# Revit family: IS_TonicII_R4340_BIM_DE
name_source: partatom
category: Plumbing Fixtures
revit_build: Autodesk Revit MEP 2016 (Build: 20161004_0715(x64)
units: mm (PartAtom-declared; Revit-internal decimal feet)

## family parameters
Always vertical = No
Cut with Voids When Loaded = No
OmniClass Number = 23.45.05.14.17.11
OmniClass Title = Shower Compartments
Part Type = Normal
Room Calculation Point = No
Round Connector Dimension = Use Diameter
Shared = No
Work Plane-Based = No

## types (1)
- R4340WG - TONIC II shelf 350x440mm
    Accessories = www.idealstandard.de\ersatzteile
    AreaUnits = millimeters
    AssetType = Fixed
    BIMObjectName = ISI_IdealStandard_Furniture_Tonic Ii_R4340WG
    BIMobject category = Storage
    BOSUseNativeGeometries = 1
    BarCode = 3391500573024
    Brand = Ideal Standard
    Brand url = http://www.idealstandard.co.uk
    Color = Glossy White
    ConnectionType = Mechanical
    CurrencyUnit = €
    Date of publishing = 06/11/2017
    Description = R4340WG TONIC II shelf 350x440mm
    DurationUnit = year
    EAN code = https://3391500573024
    Edition number = 1
    ExpectedLife = 25
    Features = TONIC II shelf 350x440mm
    Finish = Glossy White
    IFC Classification = Sanitary Terminal
    IfcExportAs = Sanitary Terminal Type
    IfcExportType = VanityUnits
    InstallationInstructions = www.idealstandard.de\produkte
    LinearUnits = millimeters
    MainColor = Glossy White
    MaintenanceInformation = www.idealstandard.de\produkte
    Manufacturer name = Ideal Standard
    ManufacturerURL = www.idealstandard.com
    Model = R4340WG
    ModelNumber = R4340WG
    ModelReference = TONIC II shelf 350x440mm
    NBS Reference Code = 35-75-94
    NBS Reference Description = Vanity Units
    Name = Furniture_Tonic Ii_R4340WG_IdealStandard
    NettWeight = 5 kg
    Nominal height = 170
    Nominal width = 350
    NominalDepth = 440 mm  [stored 1.44357 ft]
    NominalHeight = 170 mm
    NominalLength = 440 mm  [stored 1.44357 ft]
    NominalWidth = 347 mm
    Product Guid = 3416c0c4-0ad5-4c75-99fe-f1d4c0795bb9
    Product SKU = R4340
    Product data url = https://bimobject.com
    Product family = TONIC II
    Product group = Furniture
    Product name = TONIC II 350 MM OPEN SHELF GLASS WHITE
    Product url = http://www.idealspec.fr
    ProductInformation = www.idealstandard.de/produkte
    QR code = http://bimobject.com
    Shape = Rectangular
    Size = 170 x 440 x 347mm
    Space = Internal
    SpareParts = www.idealstandard.de/ersatzteile
    Technical description = http://www.idealspec.fr
    URL = www.idealstandard.com
    Uniclass 1.4 Code = L72121
    Uniclass 1.4 Description = Vanity units
    Uniclass 2.0 Code = PR-35-75-94
    Uniclass 2.0 Description = Vanity Units
    Uniclass 2015 Code = Pr_40_20_76_94
    Uniclass 2015 Name = Vanity units
    Uniclass2015Code = Pr_40_20_76_94
    Uniclass2015Title = Vanity units
    Uniclass2015Version = Products v1.1
    Version = 1
    VolumeUnits = Litres
    Weight Net (Kg) = 5

note: [stored X ft] marks values corroborated as IEEE doubles in the binary element streams (Revit-internal decimal feet)

## geometry (parser evidence)
native form markers: Blend x2, Sweep x3
no freeform markers — native parametric forms only
